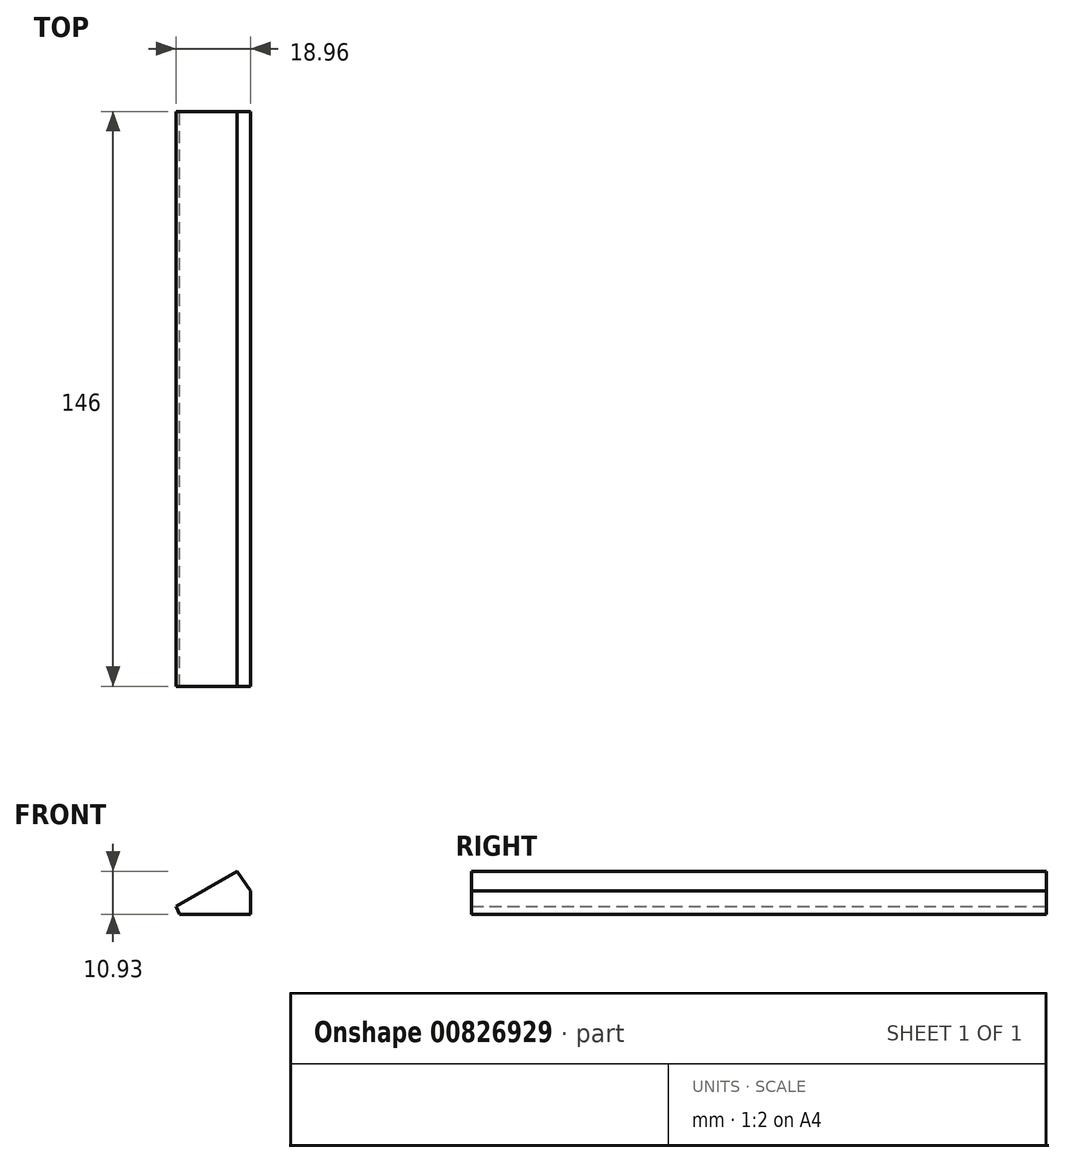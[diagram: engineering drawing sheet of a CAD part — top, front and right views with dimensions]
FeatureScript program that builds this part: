
annotation { "Feature Type Name" : "Feature", "Feature Type Description" : "" }
export const myFeature = defineFeature(function(context is Context, id is Id, definition is map)
    precondition{}
    {
        {
            var Q0;
            Q0=qCreatedBy(makeId("Front.planeOp"),FACE);
            var sketch = newSketch(context, id + "F0", { "sketchPlane" : qUnion([Q0])});
            skLineSegment(sketch, "E0", {"start": v(0, 0) * mm, "end": v(18, 0) * mm});
            skLineSegment(sketch, "E1", {"start": v(18, 0) * mm, "end": v(18, 6) * mm});
            skLineSegment(sketch, "E2", {"start": v(18, 6) * mm, "end": v(14.58, 10.93) * mm});
            skLineSegment(sketch, "E3", {"start": v(14.58, 10.93) * mm, "end": v(-0.96, 2.01) * mm});
            skLineSegment(sketch, "E4", {"start": v(0, 0) * mm, "end": v(-0.96, 2.01) * mm});
            skSolve(sketch);
        }
        {
            var Q0;
            Q0=makeQuery(id+"F0.imprint","IMPRINT",FACE,{"disambiguationData":[TD([[makeQuery(id+"F0.imprint","IMPRINT",EDGE,{"derivedFrom":sQuery(id+"F0.wireOp",EDGE,"E0")}),1.0]])]});
            extrude(context, id + "F1", {"entities" : qUnion([Q0]), "depth" : 146 * mm, "offsetDistance" : 25 * mm});
        }
    });
